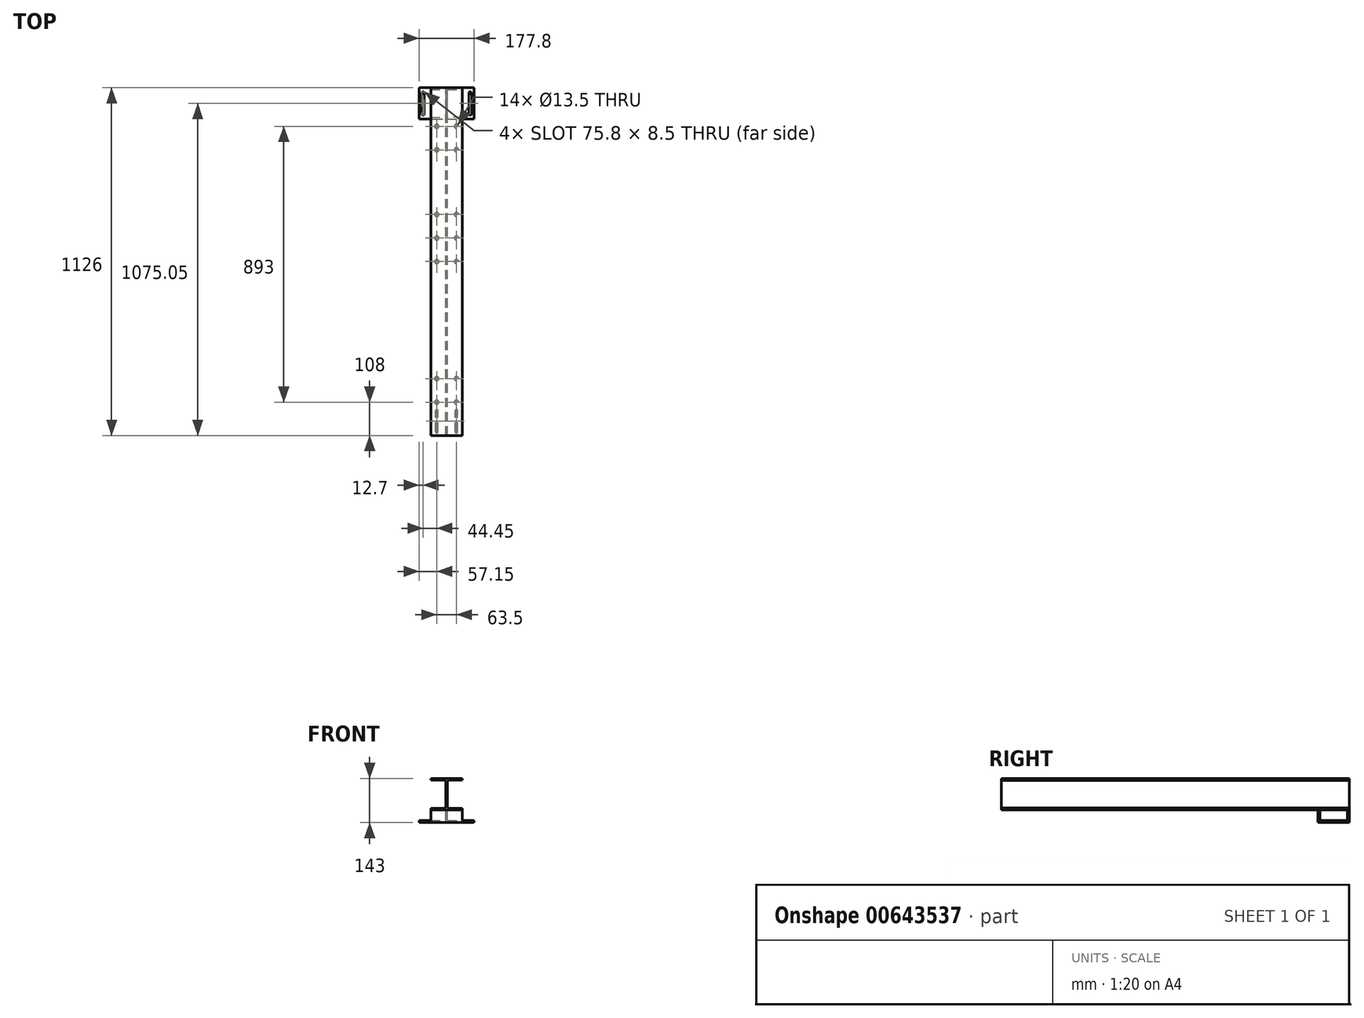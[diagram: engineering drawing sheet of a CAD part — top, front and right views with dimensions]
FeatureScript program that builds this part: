
annotation { "Feature Type Name" : "Feature", "Feature Type Description" : "" }
export const myFeature = defineFeature(function(context is Context, id is Id, definition is map)
    precondition{}
    {
        {
            var Q0;
            Q0=qCreatedBy(makeId("Front.planeOp"),FACE);
            var sketch = newSketch(context, id + "F0", { "sketchPlane" : qUnion([Q0])});
            skLineSegment(sketch, "E0", {"start": v(-51, 50.95) * mm, "end": v(51, 50.95) * mm});
            skLineSegment(sketch, "E1", {"start": v(51, 50.95) * mm, "end": v(51, 45.3) * mm});
            skLineSegment(sketch, "E2", {"start": v(51, 45.3) * mm, "end": v(2.82, 44.3) * mm});
            skLineSegment(sketch, "E3", {"start": v(2.82, 44.3) * mm, "end": v(2.83, -44.3) * mm});
            skLineSegment(sketch, "E4", {"start": v(2.82, -44.3) * mm, "end": v(51, -45.3) * mm});
            skLineSegment(sketch, "E5", {"start": v(51, -45.3) * mm, "end": v(51, -50.95) * mm});
            skLineSegment(sketch, "E6", {"start": v(51, -50.95) * mm, "end": v(-51, -50.95) * mm});
            skLineSegment(sketch, "E7", {"start": v(-51, -50.95) * mm, "end": v(-51, -45.3) * mm});
            skLineSegment(sketch, "E8", {"start": v(-51, -45.3) * mm, "end": v(-2.82, -44.3) * mm});
            skLineSegment(sketch, "E9", {"start": v(-2.83, -44.3) * mm, "end": v(-2.82, 44.3) * mm});
            skLineSegment(sketch, "E10", {"start": v(-51, 50.95) * mm, "end": v(-51, 45.3) * mm});
            skLineSegment(sketch, "E11", {"start": v(-51, 45.3) * mm, "end": v(-2.82, 44.3) * mm});
            skSolve(sketch);
        }
        {
            var Q0;
            Q0 = qSketchRegion(id + "F0", true);
            extrude(context, id + "F1", {"entities" : qUnion([Q0]), "depth" : 1126 * mm, "offsetDistance" : 25 * mm});
        }
        {
            var Q0;
            Q0=makeQuery(id+"F1.opExtrude","SWEPT_FACE",FACE,{"disambiguationData":[OSD([sQuery(id+"F0.wireOp",EDGE,"E6")])]});
            var sketch = newSketch(context, id + "F2", { "sketchPlane" : qUnion([Q0])});
            skLineSegment(sketch, "E12", {"start": v(-51, 563) * mm, "end": v(51, 563) * mm, "construction": true});
            skCircle(sketch, "E13", {"center": v(-31.75, 563) * mm, "radius": 6.75 * mm});
            skCircle(sketch, "E14.MirrorC", {"center": v(31.75, 563) * mm, "radius": 6.75 * mm});
            skLineSegment(sketch, "E15", {"start": v(-51, 486.8) * mm, "end": v(51, 486.8) * mm, "construction": true});
            skCircle(sketch, "E16", {"center": v(-31.75, 486.8) * mm, "radius": 6.75 * mm});
            skCircle(sketch, "E17.MirrorC", {"center": v(31.75, 486.8) * mm, "radius": 6.75 * mm});
            skLineSegment(sketch, "E18", {"start": v(-51, 1018) * mm, "end": v(51, 1018) * mm, "construction": true});
            skCircle(sketch, "E19", {"center": v(-31.75, 1018) * mm, "radius": 6.75 * mm});
            skCircle(sketch, "E20.MirrorC", {"center": v(31.75, 1018) * mm, "radius": 6.75 * mm});
            skLineSegment(sketch, "E21", {"start": v(-51, 941.8) * mm, "end": v(51, 941.8) * mm, "construction": true});
            skCircle(sketch, "E22", {"center": v(-31.75, 941.8) * mm, "radius": 6.75 * mm});
            skCircle(sketch, "E23.MirrorC", {"center": v(31.75, 941.8) * mm, "radius": 6.75 * mm});
            skLineSegment(sketch, "E24", {"start": v(-51, 410.6) * mm, "end": v(51, 410.6) * mm, "construction": true});
            skCircle(sketch, "E25", {"center": v(-31.75, 410.6) * mm, "radius": 6.75 * mm});
            skCircle(sketch, "E26.MirrorC", {"center": v(31.75, 410.6) * mm, "radius": 6.75 * mm});
            skArc(sketch, "E27", {"start": v(-27.5, 1113.3) * mm, "mid": v(-31.75, 1117.55) * mm, "end": v(-36, 1113.3) * mm});
            skArc(sketch, "E28", {"start": v(-36, 1046) * mm, "mid": v(-31.75, 1041.75) * mm, "end": v(-27.5, 1046) * mm});
            skLineSegment(sketch, "E29", {"start": v(-36, 1113.3) * mm, "end": v(-36, 1046) * mm});
            skLineSegment(sketch, "E30", {"start": v(-27.5, 1113.3) * mm, "end": v(-27.5, 1046) * mm});
            skArc(sketch, "E31.MirrorCS", {"start": v(27.5, 1113.3) * mm, "mid": v(31.75, 1117.55) * mm, "end": v(36, 1113.3) * mm});
            skLineSegment(sketch, "E32.MirrorCS", {"start": v(36, 1113.3) * mm, "end": v(36, 1046) * mm});
            skLineSegment(sketch, "E33.MirrorCS", {"start": v(27.5, 1113.3) * mm, "end": v(27.5, 1046) * mm});
            skArc(sketch, "E34.MirrorCS", {"start": v(36, 1046) * mm, "mid": v(31.75, 1041.75) * mm, "end": v(27.5, 1046) * mm});
            skLineSegment(sketch, "E35", {"start": v(-51, 201.2) * mm, "end": v(51, 201.2) * mm, "construction": true});
            skCircle(sketch, "E36", {"center": v(-31.75, 201.2) * mm, "radius": 6.75 * mm});
            skCircle(sketch, "E37.MirrorC", {"center": v(31.75, 201.2) * mm, "radius": 6.75 * mm});
            skLineSegment(sketch, "E38", {"start": v(-51, 125) * mm, "end": v(51, 125) * mm, "construction": true});
            skCircle(sketch, "E39", {"center": v(-31.75, 125) * mm, "radius": 6.75 * mm});
            skCircle(sketch, "E40.MirrorC", {"center": v(31.75, 125) * mm, "radius": 6.75 * mm});
            skLineSegment(sketch, "E41.bottom", {"start": v(-51, 213.9) * mm, "end": v(50.6, 213.9) * mm, "construction": true});
            skLineSegment(sketch, "E41.top", {"start": v(-51, 112.3) * mm, "end": v(50.6, 112.3) * mm, "construction": true});
            skLineSegment(sketch, "E42", {"start": v(-51, 163.1) * mm, "end": v(51, 163.1) * mm, "construction": true});
            skSolve(sketch);
        }
        {
            var Q0;
            Q0 = qSketchRegion(id + "F2", true);
            extrude(context, id + "F3", {"entities" : qUnion([Q0]), "operationType" : NewBodyOperationType.REMOVE, "endBound" : BoundingType.UP_TO_NEXT, "oppositeDirection" : true, "depth" : 25 * mm, "offsetDistance" : 25 * mm});
        }
        {
            var Q0;
            Q0=makeQuery(id+"F1.opExtrude","SWEPT_FACE",FACE,{"disambiguationData":[OSD([sQuery(id+"F0.wireOp",EDGE,"E6")])]});
            var sketch = newSketch(context, id + "F4", { "sketchPlane" : qUnion([Q0])});
            skLineSegment(sketch, "E43", {"start": v(-51, 101.9) * mm, "end": v(51, 101.9) * mm});
            skLineSegment(sketch, "E44", {"start": v(51, 101.9) * mm, "end": v(51, 96.25) * mm});
            skLineSegment(sketch, "E45", {"start": v(51, 96.25) * mm, "end": v(2.82, 95.25) * mm});
            skLineSegment(sketch, "E46", {"start": v(2.82, 95.25) * mm, "end": v(2.83, 6.65) * mm});
            skLineSegment(sketch, "E47", {"start": v(2.82, 6.65) * mm, "end": v(51, 5.65) * mm});
            skLineSegment(sketch, "E48", {"start": v(51, 5.65) * mm, "end": v(51, 0) * mm});
            skLineSegment(sketch, "E49", {"start": v(51, 0) * mm, "end": v(-51, 0) * mm});
            skLineSegment(sketch, "E50", {"start": v(-51, 0) * mm, "end": v(-51, 5.65) * mm});
            skLineSegment(sketch, "E51", {"start": v(-51, 5.65) * mm, "end": v(-2.82, 6.65) * mm});
            skLineSegment(sketch, "E52", {"start": v(-2.83, 6.65) * mm, "end": v(-2.82, 95.25) * mm});
            skLineSegment(sketch, "E53", {"start": v(-51, 101.9) * mm, "end": v(-51, 96.25) * mm});
            skLineSegment(sketch, "E54", {"start": v(-51, 96.25) * mm, "end": v(-2.82, 95.25) * mm});
            skSolve(sketch);
        }
        {
            var Q0;
            Q0 = qSketchRegion(id + "F4", true);
            extrude(context, id + "F5", {"entities" : qUnion([Q0]), "operationType" : NewBodyOperationType.ADD, "depth" : 34.7 * mm, "offsetDistance" : 25 * mm});
        }
        {
            var Q0;
            Q0=makeQuery(id+"F5.opExtrude","CAP_FACE",FACE,{"disambiguationData":[OSD([sQuery(id+"F4.wireOp",EDGE,"E43"),sQuery(id+"F4.wireOp",EDGE,"E44"),sQuery(id+"F4.wireOp",EDGE,"E45"),sQuery(id+"F4.wireOp",EDGE,"E46"),sQuery(id+"F4.wireOp",EDGE,"E47"),sQuery(id+"F4.wireOp",EDGE,"E48"),sQuery(id+"F4.wireOp",EDGE,"E49"),sQuery(id+"F4.wireOp",EDGE,"E50"),sQuery(id+"F4.wireOp",EDGE,"E51"),sQuery(id+"F4.wireOp",EDGE,"E52"),sQuery(id+"F4.wireOp",EDGE,"E53"),sQuery(id+"F4.wireOp",EDGE,"E54")])],"isStart":false});
            var sketch = newSketch(context, id + "F6", { "sketchPlane" : qUnion([Q0])});
            skLineSegment(sketch, "E55.bottom", {"start": v(-88.9, 0) * mm, "end": v(88.9, 0) * mm});
            skLineSegment(sketch, "E55.top", {"start": v(-88.9, 101.9) * mm, "end": v(88.9, 101.9) * mm});
            skLineSegment(sketch, "E55.left", {"start": v(-88.9, 0) * mm, "end": v(-88.9, 101.9) * mm});
            skLineSegment(sketch, "E55.right", {"start": v(88.9, 0) * mm, "end": v(88.9, 101.9) * mm});
            skSolve(sketch);
        }
        {
            var Q0;
            Q0 = qSketchRegion(id + "F6", true);
            extrude(context, id + "F7", {"entities" : qUnion([Q0]), "operationType" : NewBodyOperationType.ADD, "depth" : 6.4 * mm, "offsetDistance" : 25 * mm});
        }
        {
            var Q0;
            Q0=makeQuery(id+"F7.opExtrude","CAP_FACE",FACE,{"disambiguationData":[OSD([sQuery(id+"F6.wireOp",EDGE,"E55.bottom"),sQuery(id+"F6.wireOp",EDGE,"E55.top"),sQuery(id+"F6.wireOp",EDGE,"E55.left"),sQuery(id+"F6.wireOp",EDGE,"E55.right")])],"isStart":false});
            var sketch = newSketch(context, id + "F8", { "sketchPlane" : qUnion([Q0])});
            skArc(sketch, "E56", {"start": v(-71.95, 84.6) * mm, "mid": v(-76.2, 88.85) * mm, "end": v(-80.45, 84.6) * mm});
            skArc(sketch, "E57", {"start": v(-80.45, 17.3) * mm, "mid": v(-76.2, 13.05) * mm, "end": v(-71.95, 17.3) * mm});
            skLineSegment(sketch, "E58", {"start": v(-80.45, 84.6) * mm, "end": v(-80.45, 17.3) * mm});
            skLineSegment(sketch, "E59", {"start": v(-71.95, 84.6) * mm, "end": v(-71.95, 17.3) * mm});
            skLineSegment(sketch, "E60", {"start": v(-88.9, 50.95) * mm, "end": v(88.9, 50.95) * mm, "construction": true});
            skArc(sketch, "E61.MirrorCS", {"start": v(71.95, 84.6) * mm, "mid": v(76.2, 88.85) * mm, "end": v(80.45, 84.6) * mm});
            skLineSegment(sketch, "E62.MirrorCS", {"start": v(71.95, 84.6) * mm, "end": v(71.95, 17.3) * mm});
            skLineSegment(sketch, "E63.MirrorCS", {"start": v(80.45, 84.6) * mm, "end": v(80.45, 17.3) * mm});
            skArc(sketch, "E64.MirrorCS", {"start": v(80.45, 17.3) * mm, "mid": v(76.2, 13.05) * mm, "end": v(71.95, 17.3) * mm});
            skSolve(sketch);
        }
        {
            var Q0;
            Q0 = qSketchRegion(id + "F8", true);
            extrude(context, id + "F9", {"entities" : qUnion([Q0]), "operationType" : NewBodyOperationType.REMOVE, "endBound" : BoundingType.UP_TO_NEXT, "oppositeDirection" : true, "depth" : 25 * mm, "offsetDistance" : 25 * mm});
        }
    });
